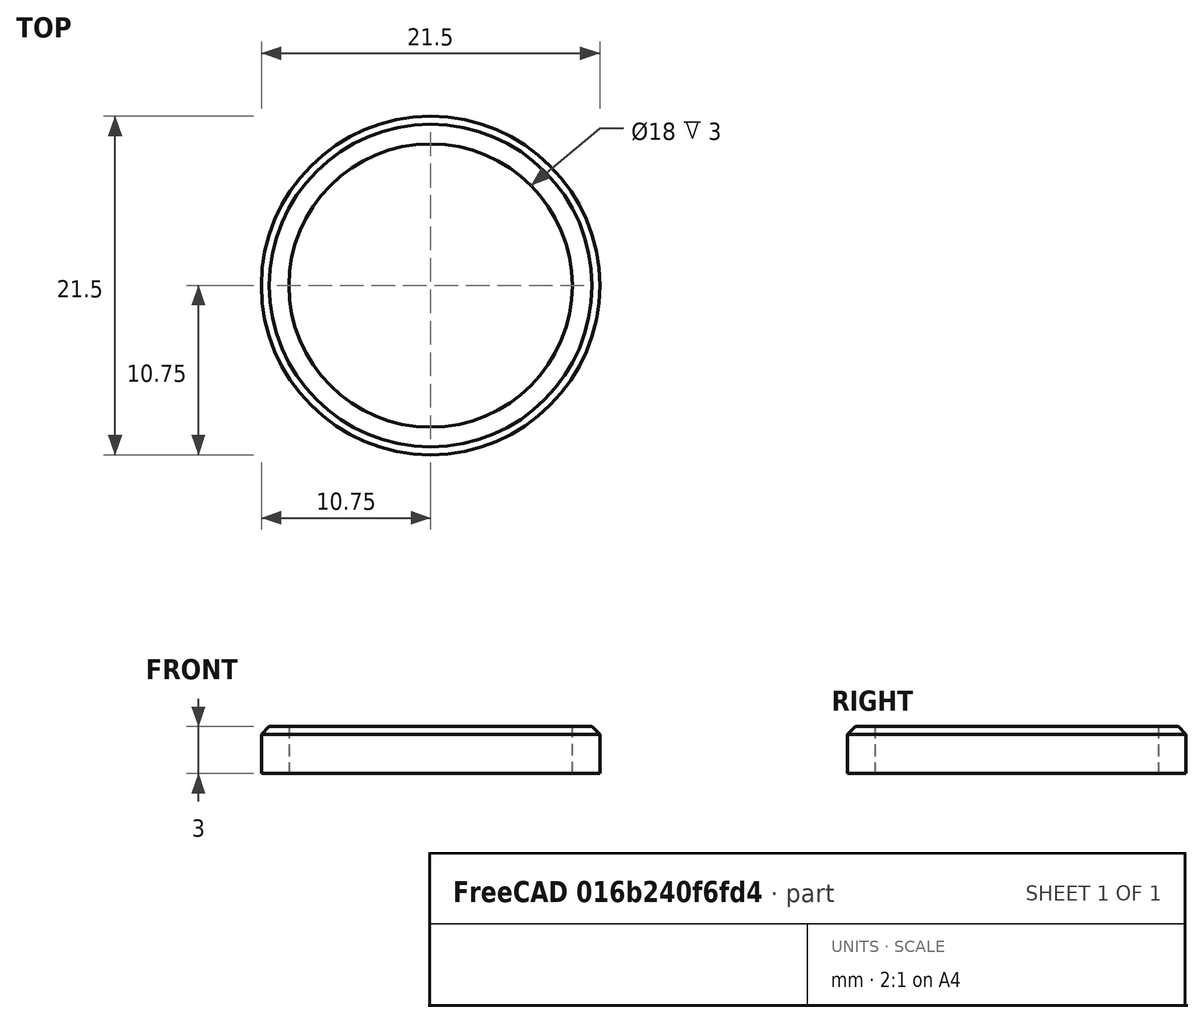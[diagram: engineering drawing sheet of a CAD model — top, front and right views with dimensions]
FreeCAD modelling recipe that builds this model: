
FCSTD DOCUMENT  (FreeCAD 0.19R24276 (Git))
Label: ring_d21_5__d18
License: All rights reserved
LicenseURL: http://en.wikipedia.org/wiki/All_rights_reserved
objects: Sketcher::SketchObject×1, PartDesign::Pad×1, PartDesign::Chamfer×1, PartDesign::Body×1
note: 6 computed .brp shape members not serialized (recipe doc carries the construction recipe); baked Part::Feature solids carry a one-line shape summary decoded from their .brp

FEATURE [Sketcher::SketchObject] Sketch  label="Sketch_d18_d21,5"
  FullyConstrained = true
  MapMode = 5
  Support = -> [XY_Plane]
  sketch-geometry (2):
    g0: Circle CenterX=0 CenterY=0 CenterZ=0 NormalX=0 NormalY=0 NormalZ=1 AngleXU=0 Radius=10.75
    g1: Circle CenterX=0 CenterY=0 CenterZ=0 NormalX=0 NormalY=0 NormalZ=1 AngleXU=0 Radius=9
  constraints (4):
    c: Coincident(g0,g-1)
    c: Coincident(g1,g-1)
    c: Diameter(g0) = 21.5
    c: Diameter(g1) = 18
FEATURE [PartDesign::Pad] Pad  label="Pad_h3"
  Direction = (1,1,1)
  Length = 3
  Length2 = 100
  Profile = -> Sketch
  Type = 0
FEATURE [PartDesign::Chamfer] Chamfer
  Angle = 45
  Base = -> Pad [Edge3]
  BaseFeature = -> Pad
  ChamferType = 0
  FlipDirection = false
  Size = 0.5
  Size2 = 1
  SupportTransform = false
FEATURE [PartDesign::Body] Body
  Group = -> [Sketch,Pad,Chamfer]
  Origin = -> Origin
  Tip = -> Chamfer
